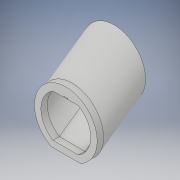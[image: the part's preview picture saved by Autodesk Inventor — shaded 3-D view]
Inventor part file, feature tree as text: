
AUTODESK INVENTOR PART (.ipt)
format: ipt  version: 2017 (Build 210142000, 142)  size: 194,560 bytes
history: native  units: in
note: dims shown in document units (in); Inventor stores cm internally (conversion verified against a paired STEP export)
features: sketch x2, sweep x2, extrude x2, plane x1
ambient origin geometry x8: Origin, YZ Plane, XZ Plane, XY Plane, X Axis, Y Axis, Z Axis, Center Point
bodies: Solid1 (feature_tree), Solid2 (feature_tree), Solid3 (feature_tree)
feature tree (7):
  sketch  "Sketch1"  dims[d0=6.6667in d1=4.0in d2=1.0in d28=8.0in]
  plane  "Work Plane2"
  sketch  "Sketch6"  dims[d29=0.3779in d30=0.0in d31=0.0in d32=1.0in d33=0.0in d34=0.5833in d35=0.0625in d36=0.0625in d37=0.125in d38=0.25in d39=0.125in d40=45.0deg d41=0.0892in d42=0.0884in d43=0.0in d44=0.0in d45=1.0in d46=0.0in]
  sweep  "ramp"
  sweep  "light angle"
  extrude  "connection bottom"  Depth=1.0in TaperAngle=0.0deg
  extrude  "light flat"  Depth=0.5833in
